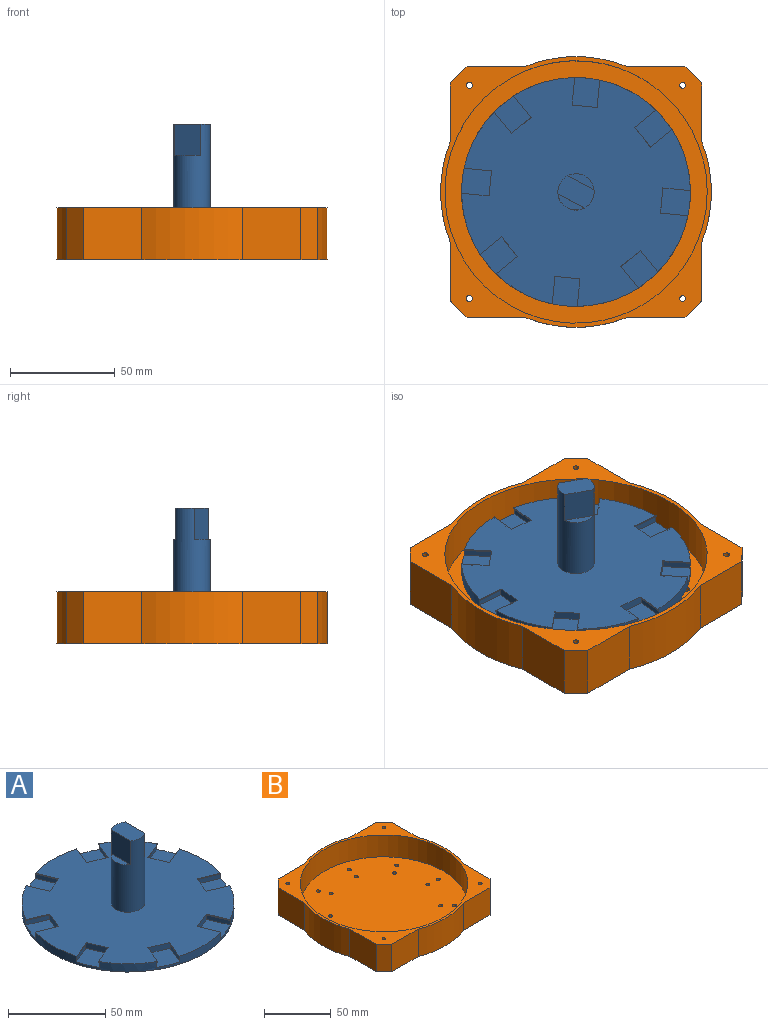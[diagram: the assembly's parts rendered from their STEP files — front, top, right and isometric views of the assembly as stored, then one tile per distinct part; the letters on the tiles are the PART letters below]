
ASSEMBLY  parts=2 mates=1
PART A: 90 faces, bbox 109.2x109.2x50 mm
  f0: plane 17.3x10mm, normal (0,0,1), area 162.8mm2, adj f85,f86,f88
  f1: plane 12.01x4.98mm, normal (-0.38,0.92,0), area 47.2mm2, adj f2,f3,f27,f36,f79,f81,f82,f84
  f2: plane 12.14x5.03mm, normal (-0.92,-0.38,0), area 41.7mm2, adj f1,f25,f36,f84
  f3: plane 12.14x5.03mm, normal (0.92,0.38,0), area 41.7mm2, adj f1,f25,f36,f81
  f4: plane 12.01x4.98mm, normal (0.38,0.92,0), area 47.2mm2, adj f5,f6,f27,f35,f73,f75,f76,f78
  f5: plane 12.14x5.03mm, normal (0.92,-0.38,0), area 41.7mm2, adj f4,f25,f35,f78
  f6: plane 12.14x5.03mm, normal (-0.92,0.38,0), area 41.7mm2, adj f4,f25,f35,f75
  f7: plane 12.01x4.98mm, normal (0.92,0.38,0), area 47.2mm2, adj f8,f9,f27,f34,f67,f69,f70,f72
  f8: plane 12.14x5.03mm, normal (0.38,-0.92,0), area 41.7mm2, adj f7,f25,f34,f72
  f9: plane 12.14x5.03mm, normal (-0.38,0.92,0), area 41.7mm2, adj f7,f25,f34,f69
  f10: plane 12.01x4.98mm, normal (0.92,-0.38,0), area 47.2mm2, adj f11,f12,f27,f33,f61,f63,f64,f66
  f11: plane 12.14x5.03mm, normal (-0.38,-0.92,0), area 41.7mm2, adj f10,f25,f33,f66
  f12: plane 12.14x5.03mm, normal (0.38,0.92,0), area 41.7mm2, adj f10,f25,f33,f63
  f13: plane 12.01x4.98mm, normal (0.38,-0.92,0), area 47.2mm2, adj f14,f15,f27,f32,f55,f57,f58,f60
  f14: plane 12.14x5.03mm, normal (0.92,0.38,0), area 41.7mm2, adj f13,f25,f32,f60
  f15: plane 12.14x5.03mm, normal (-0.92,-0.38,0), area 41.7mm2, adj f13,f25,f32,f57
  f16: plane 12.01x4.98mm, normal (-0.38,-0.92,0), area 47.2mm2, adj f17,f18,f27,f31,f49,f51,f52,f54
  f17: plane 12.14x5.03mm, normal (-0.92,0.38,0), area 41.7mm2, adj f16,f25,f31,f54
  f18: plane 12.14x5.03mm, normal (0.92,-0.38,0), area 41.7mm2, adj f16,f25,f31,f51
  f19: plane 12.01x4.98mm, normal (-0.92,-0.38,0), area 47.2mm2, adj f20,f21,f27,f30,f43,f45,f46,f48
  f20: plane 12.14x5.03mm, normal (0.38,-0.92,0), area 41.7mm2, adj f19,f25,f30,f48
  f21: plane 12.14x5.03mm, normal (-0.38,0.92,0), area 41.7mm2, adj f19,f25,f30,f45
  f22: plane 12.01x4.98mm, normal (-0.92,0.38,0), area 47.2mm2, adj f23,f24,f27,f29,f37,f39,f40,f42
  f23: plane 12.14x5.03mm, normal (0.38,0.92,0), area 41.7mm2, adj f22,f25,f29,f42
  f24: plane 12.14x5.03mm, normal (-0.38,-0.92,0), area 41.7mm2, adj f22,f25,f29,f39
  f25: cylinder r=54.59mm len=109.19mm, axis (0,0,-1), area 1394.6mm2, adj f2,f3,f5,f6,f8,f9,f11,f12
  f26: cylinder r=54.59mm len=0.5mm, axis (0,0,-1), area 0.2mm2, adj f25,f27,f47,f48
  f27: plane 109.19x109.19mm, normal (0,0,1), area 7840.6mm2, adj f1,f4,f7,f10,f13,f16,f19,f22
  f28: plane 109.19x109.19mm, normal (0,0,-1), area 9363.8mm2, adj f25
  f29: plane 17.11x17.04mm, normal (0,0,1), area 174.2mm2, adj f22,f23,f24,f25
  f30: plane 17.11x17.04mm, normal (0,0,1), area 174.2mm2, adj f19,f20,f21,f25
  f31: plane 17.11x17.04mm, normal (0,0,1), area 174.2mm2, adj f16,f17,f18,f25
  f32: plane 17.11x17.04mm, normal (0,0,1), area 174.2mm2, adj f13,f14,f15,f25
  f33: plane 17.11x17.04mm, normal (0,0,1), area 174.2mm2, adj f10,f11,f12,f25
  f34: plane 17.11x17.04mm, normal (0,0,1), area 174.2mm2, adj f7,f8,f9,f25
  f35: plane 17.11x17.04mm, normal (0,0,1), area 174.2mm2, adj f4,f5,f6,f25
  f36: plane 17.11x17.04mm, normal (0,0,1), area 174.2mm2, adj f1,f2,f3,f25
  f37: plane 12.14x5.03mm, normal (-0.38,-0.92,0), area 6.6mm2, adj f22,f27,f38,f39
  f38: plane 0.5x0.05mm, normal (-0.46,-0.89,0), area 0mm2, adj f25,f27,f37,f39
  f39: plane 12.38x5.49mm, normal (0,0,-1), area 6.6mm2, adj f22,f24,f25,f37,f38
  f40: plane 12.14x5.03mm, normal (0.38,0.92,0), area 6.6mm2, adj f22,f27,f41,f42
  f41: plane 0.5x0.05mm, normal (0.33,0.94,0), area 0mm2, adj f25,f27,f40,f42
  f42: plane 12.33x5.51mm, normal (0,0,-1), area 6.6mm2, adj f22,f23,f25,f40,f41
  f43: plane 12.14x5.03mm, normal (-0.38,0.92,0), area 6.6mm2, adj f19,f27,f44,f45
  f44: plane 0.5x0.05mm, normal (-0.45,0.89,0), area 0mm2, adj f25,f27,f43,f45
  f45: plane 12.38x5.49mm, normal (0,0,-1), area 6.6mm2, adj f19,f21,f25,f43,f44
  f46: plane 12.14x5.03mm, normal (0.38,-0.92,0), area 6.6mm2, adj f19,f27,f47,f48
  f47: plane 0.5x0.05mm, normal (0.31,-0.95,0), area 0mm2, adj f26,f27,f46,f48
  f48: plane 12.33x5.51mm, normal (0,0,-1), area 6.6mm2, adj f19,f20,f26,f46,f47
  f49: plane 12.14x5.03mm, normal (0.92,-0.38,0), area 6.6mm2, adj f16,f27,f50,f51
  f50: plane 0.5x0.05mm, normal (0.9,-0.44,0), area 0mm2, adj f25,f27,f49,f51
  f51: plane 12.38x5.49mm, normal (0,0,-1), area 6.6mm2, adj f16,f18,f25,f49,f50
  f52: plane 12.14x5.03mm, normal (-0.92,0.38,0), area 6.6mm2, adj f16,f27,f53,f54
  f53: plane 0.5x0.05mm, normal (-0.95,0.32,0), area 0mm2, adj f25,f27,f52,f54
  f54: plane 12.33x5.51mm, normal (0,0,-1), area 6.6mm2, adj f16,f17,f25,f52,f53
  f55: plane 12.14x5.03mm, normal (-0.92,-0.38,0), area 6.6mm2, adj f13,f27,f56,f57
  f56: plane 0.5x0.05mm, normal (-0.9,-0.44,0), area 0mm2, adj f25,f27,f55,f57
  f57: plane 12.38x5.49mm, normal (0,0,-1), area 6.6mm2, adj f13,f15,f25,f55,f56
  f58: plane 12.14x5.03mm, normal (0.92,0.38,0), area 6.6mm2, adj f13,f27,f59,f60
  f59: plane 0.5x0.05mm, normal (0.95,0.32,0), area 0mm2, adj f25,f27,f58,f60
  f60: plane 12.33x5.51mm, normal (0,0,-1), area 6.6mm2, adj f13,f14,f25,f58,f59
  f61: plane 12.14x5.03mm, normal (0.38,0.92,0), area 6.6mm2, adj f10,f27,f62,f63
  f62: plane 0.5x0.05mm, normal (0.44,0.9,0), area 0mm2, adj f25,f27,f61,f63
  f63: plane 12.38x5.49mm, normal (0,0,-1), area 6.6mm2, adj f10,f12,f25,f61,f62
  f64: plane 12.14x5.03mm, normal (-0.38,-0.92,0), area 6.6mm2, adj f10,f27,f65,f66
  f65: plane 0.5x0.05mm, normal (-0.32,-0.95,0), area 0mm2, adj f25,f27,f64,f66
  f66: plane 12.33x5.51mm, normal (0,0,-1), area 6.6mm2, adj f10,f11,f25,f64,f65
  f67: plane 12.14x5.03mm, normal (-0.38,0.92,0), area 6.6mm2, adj f7,f27,f68,f69
  f68: plane 0.5x0.05mm, normal (-0.31,0.95,0), area 0mm2, adj f25,f27,f67,f69
  f69: plane 12.33x5.51mm, normal (0,0,-1), area 6.6mm2, adj f7,f9,f25,f67,f68
  f70: plane 12.14x5.03mm, normal (0.38,-0.92,0), area 6.6mm2, adj f7,f27,f71,f72
  f71: plane 0.5x0.05mm, normal (0.47,-0.88,0), area 0mm2, adj f25,f27,f70,f72
  f72: plane 12.38x5.49mm, normal (0,0,-1), area 6.6mm2, adj f7,f8,f25,f70,f71
  f73: plane 12.14x5.03mm, normal (-0.92,0.38,0), area 6.6mm2, adj f4,f27,f74,f75
  f74: plane 0.5x0.05mm, normal (-0.9,0.43,0), area 0mm2, adj f25,f27,f73,f75
  f75: plane 12.38x5.49mm, normal (0,0,-1), area 6.6mm2, adj f4,f6,f25,f73,f74
  f76: plane 12.14x5.03mm, normal (0.92,-0.38,0), area 6.6mm2, adj f4,f27,f77,f78
  f77: plane 0.5x0.05mm, normal (0.95,-0.32,0), area 0mm2, adj f25,f27,f76,f78
  f78: plane 12.33x5.51mm, normal (0,0,-1), area 6.6mm2, adj f4,f5,f25,f76,f77
  f79: plane 12.14x5.03mm, normal (0.92,0.38,0), area 6.6mm2, adj f1,f27,f80,f81
  f80: plane 0.5x0.05mm, normal (0.92,0.4,0), area 0mm2, adj f25,f27,f79,f81
  f81: plane 12.38x5.49mm, normal (0,0,-1), area 6.6mm2, adj f1,f3,f25,f79,f80
  f82: plane 12.14x5.03mm, normal (-0.92,-0.38,0), area 6.6mm2, adj f1,f27,f83,f84
  f83: plane 0.5x0.05mm, normal (-0.95,-0.31,0), area 0mm2, adj f25,f27,f82,f84
  f84: plane 12.33x5.51mm, normal (0,0,-1), area 6.6mm2, adj f1,f2,f25,f82,f83
  f85: cylinder r=8.65mm len=44.83mm, axis (0,0,-1), area 1941.1mm2, adj f0,f27,f86,f87,f88,f89
  f86: plane 15x14.12mm, normal (-1,0,0), area 211.8mm2, adj f0,f85,f87
  f87: plane 14.12x3.65mm, normal (0,0,1), area 36.1mm2, adj f85,f86
  f88: plane 15x14.12mm, normal (1,0,0), area 211.8mm2, adj f0,f85,f89
  f89: plane 14.12x3.65mm, normal (0,0,1), area 36.1mm2, adj f85,f88
PART B: 60 faces, bbox 129.2x129.2x25 mm
  f0: cylinder r=1.5mm len=3mm, axis (0,0,-1), area 28.3mm2, adj f18,f46
  f1: cylinder r=1.5mm len=3mm, axis (0,0,-1), area 28.3mm2, adj f18,f49
  f2: cylinder r=1.5mm len=3mm, axis (0,0,-1), area 28.3mm2, adj f18,f48
  f3: cylinder r=1.5mm len=3mm, axis (0,0,-1), area 28.3mm2, adj f18,f51
  f4: cylinder r=1.5mm len=3mm, axis (0,0,-1), area 28.3mm2, adj f18,f50
  f5: cylinder r=1.5mm len=3mm, axis (0,0,-1), area 28.3mm2, adj f18,f59
  f6: cylinder r=1.5mm len=3mm, axis (0,0,-1), area 28.3mm2, adj f18,f58
  f7: cylinder r=1.5mm len=3mm, axis (0,0,-1), area 28.3mm2, adj f18,f57
  f8: cylinder r=1.5mm len=3mm, axis (0,0,-1), area 28.3mm2, adj f18,f56
  f9: cylinder r=1.5mm len=3mm, axis (0,0,-1), area 28.3mm2, adj f18,f55
  f10: cylinder r=1.5mm len=3mm, axis (0,0,-1), area 28.3mm2, adj f18,f54
  f11: cylinder r=1.5mm len=3mm, axis (0,0,-1), area 28.3mm2, adj f18,f53
  f12: cylinder r=1.5mm len=3mm, axis (0,0,-1), area 28.3mm2, adj f18,f52
  f13: cylinder r=1.5mm len=3mm, axis (0,0,-1), area 28.3mm2, adj f18,f43
  f14: cylinder r=1.5mm len=3mm, axis (0,0,-1), area 28.3mm2, adj f18,f42
  f15: cylinder r=1.5mm len=3mm, axis (0,0,-1), area 28.3mm2, adj f18,f45
  f16: cylinder r=1.5mm len=3mm, axis (0,0,-1), area 28.3mm2, adj f18,f44
  f17: cylinder r=1.5mm len=3mm, axis (0,0,-1), area 28.3mm2, adj f18,f47
  f18: plane 125.19x125.19mm, normal (0,0,1), area 12181.9mm2, adj f0,f1,f2,f3,f4,f5,f6,f7
  f19: plane 129.19x129.19mm, normal (0,0,-1), area 14145.3mm2, adj f20,f21,f22,f23,f24,f25,f26,f27
  f20: plane 28.07x25mm, normal (-1,0,0), area 701.8mm2, adj f19,f21,f38,f41
  f21: cylinder r=64.59mm len=47.85mm, axis (0,0,-1), area 1225.6mm2, adj f19,f20,f22,f41
  f22: plane 28.07x25mm, normal (-1,0,0), area 701.8mm2, adj f19,f21,f23,f41
  f23: plane 25x8mm, normal (-0.71,-0.71,0), area 282.8mm2, adj f19,f22,f24,f41
  f24: plane 28.07x25mm, normal (0,-1,0), area 701.8mm2, adj f19,f23,f25,f41
  f25: cylinder r=64.59mm len=47.85mm, axis (0,0,-1), area 1225.6mm2, adj f19,f24,f26,f41
  f26: plane 28.07x25mm, normal (0,-1,0), area 701.8mm2, adj f19,f25,f27,f41
  f27: plane 25x8mm, normal (0.71,-0.71,0), area 282.8mm2, adj f19,f26,f28,f41
  f28: plane 28.07x25mm, normal (1,0,0), area 701.8mm2, adj f19,f27,f29,f41
  f29: cylinder r=64.59mm len=47.85mm, axis (0,0,-1), area 1225.6mm2, adj f19,f28,f30,f41
  f30: plane 28.07x25mm, normal (1,0,0), area 701.8mm2, adj f19,f29,f31,f41
  f31: plane 25x8mm, normal (0.71,0.71,0), area 282.8mm2, adj f19,f30,f32,f41
  f32: plane 28.07x25mm, normal (0,1,0), area 701.8mm2, adj f19,f31,f33,f41
  f33: cylinder r=64.59mm len=47.85mm, axis (0,0,-1), area 1225.6mm2, adj f19,f32,f34,f41
  f34: plane 28.07x25mm, normal (0,1,0), area 701.8mm2, adj f19,f33,f38,f41
  f35: cylinder r=1.4mm len=25mm, axis (0,0,-1), area 219.9mm2, adj f19,f41
  f36: cylinder r=1.4mm len=25mm, axis (0,0,-1), area 219.9mm2, adj f19,f41
  f37: cylinder r=1.4mm len=25mm, axis (0,0,-1), area 219.9mm2, adj f19,f41
  f38: plane 25x8mm, normal (-0.71,0.71,0), area 282.8mm2, adj f19,f20,f34,f41
  f39: cylinder r=62.59mm len=125.19mm, axis (0,0,-1), area 7865.9mm2, adj f18,f41
  f40: cylinder r=1.4mm len=25mm, axis (0,0,-1), area 219.9mm2, adj f19,f41
  f41: plane 129.19x129.19mm, normal (0,0,1), area 2528.9mm2, adj f20,f21,f22,f23,f24,f25,f26,f27
  f42: torus R=3.5mm, axis (0,0,1), area 44mm2, adj f14,f19
  f43: torus R=3.5mm, axis (0,0,1), area 44mm2, adj f13,f19
  f44: torus R=3.5mm, axis (0,0,1), area 44mm2, adj f16,f19
  f45: torus R=3.5mm, axis (0,0,1), area 44mm2, adj f15,f19
  f46: torus R=3.5mm, axis (0,0,1), area 44mm2, adj f0,f19
  f47: torus R=3.5mm, axis (0,0,1), area 44mm2, adj f17,f19
  f48: torus R=3.5mm, axis (0,0,1), area 44mm2, adj f2,f19
  f49: torus R=3.5mm, axis (0,0,1), area 44mm2, adj f1,f19
  f50: torus R=3.5mm, axis (0,0,1), area 44mm2, adj f4,f19
  f51: torus R=3.5mm, axis (0,0,1), area 44mm2, adj f3,f19
  f52: torus R=3.5mm, axis (0,0,1), area 44mm2, adj f12,f19
  f53: torus R=3.5mm, axis (0,0,1), area 44mm2, adj f11,f19
  f54: torus R=3.5mm, axis (0,0,1), area 44mm2, adj f10,f19
  f55: torus R=3.5mm, axis (0,0,1), area 44mm2, adj f9,f19
  f56: torus R=3.5mm, axis (0,0,1), area 44mm2, adj f8,f19
  f57: torus R=3.5mm, axis (0,0,1), area 44mm2, adj f7,f19
  f58: torus R=3.5mm, axis (0,0,1), area 44mm2, adj f6,f19
  f59: torus R=3.5mm, axis (0,0,1), area 44mm2, adj f5,f19
PLACE A rot(axis=(0,0,-1),118.2deg) t=(-40.33,-52.07,-2.65)mm
PLACE B t=(-40.33,-52.07,-17.48)mm fixed
MATE revolute B.f39 <-> A.f85  axis (0,0,1) through (-40.33,-52.07,-12.48)mm
